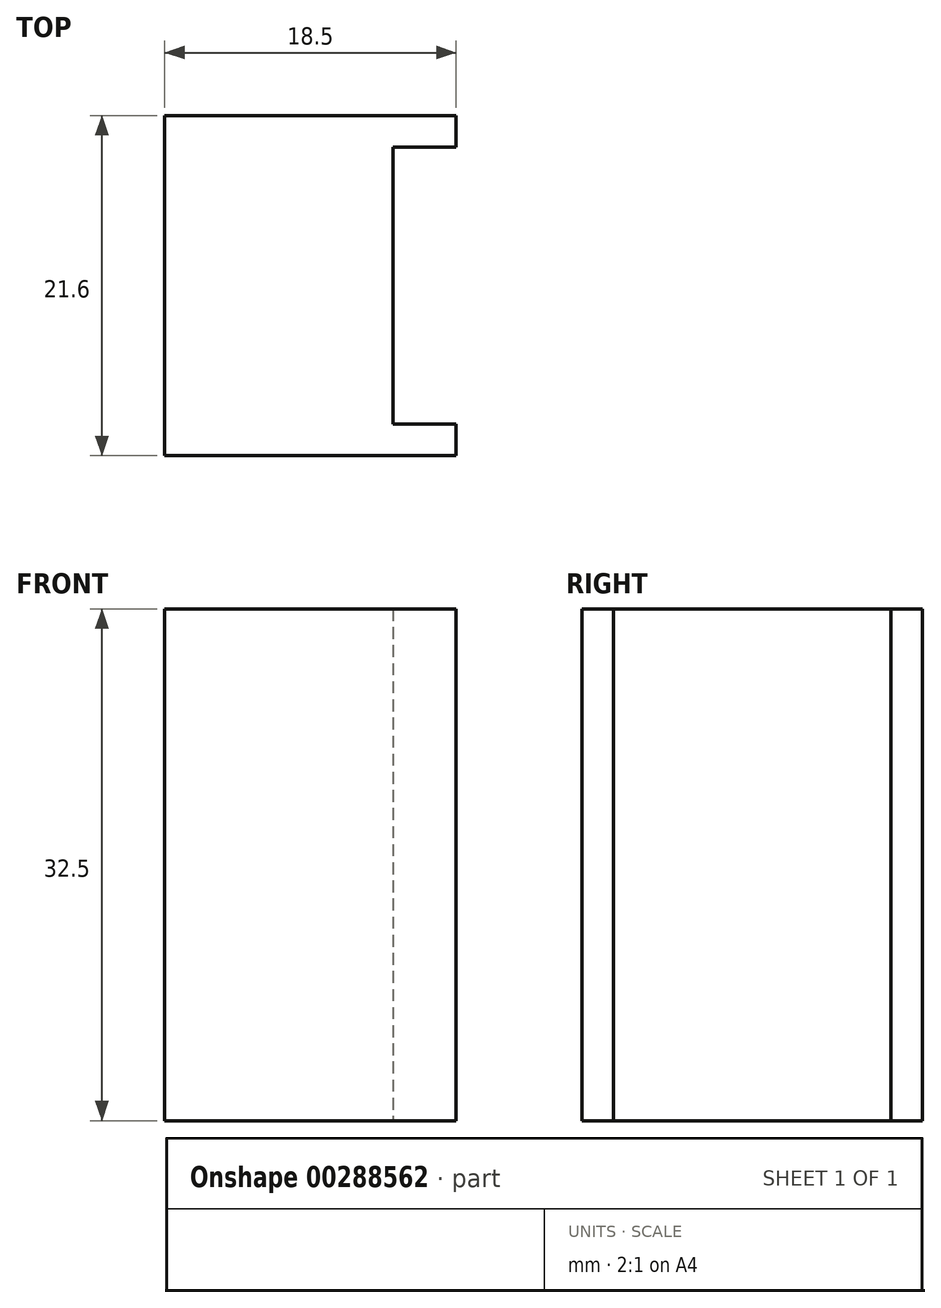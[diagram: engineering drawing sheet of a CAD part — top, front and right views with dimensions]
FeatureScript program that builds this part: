
annotation { "Feature Type Name" : "Feature", "Feature Type Description" : "" }
export const myFeature = defineFeature(function(context is Context, id is Id, definition is map)
    precondition{}
    {
        {
            var Q0;
            Q0=qCreatedBy(makeId("Top.planeOp"),FACE);
            var sketch = newSketch(context, id + "F0", { "sketchPlane" : qUnion([Q0])});
            skLineSegment(sketch, "E0.bottom", {"start": v(7.25, 10.8) * mm, "end": v(-7.25, 10.8) * mm});
            skLineSegment(sketch, "E0.top", {"start": v(7.25, -10.8) * mm, "end": v(-7.25, -10.8) * mm});
            skLineSegment(sketch, "E0.left", {"start": v(7.25, 10.8) * mm, "end": v(7.25, -10.8) * mm});
            skLineSegment(sketch, "E0.right", {"start": v(-7.25, 10.8) * mm, "end": v(-7.25, -10.8) * mm});
            skPoint(sketch, "E0.middle", {"position": v(0, 0) * mm});
            skLineSegment(sketch, "E1.bottom", {"start": v(7.25, 10.8) * mm, "end": v(11.25, 10.8) * mm});
            skLineSegment(sketch, "E1.top", {"start": v(7.25, 8.8) * mm, "end": v(11.25, 8.8) * mm});
            skLineSegment(sketch, "E1.left", {"start": v(7.25, 10.8) * mm, "end": v(7.25, 8.8) * mm});
            skLineSegment(sketch, "E1.right", {"start": v(11.25, 10.8) * mm, "end": v(11.25, 8.8) * mm});
            skLineSegment(sketch, "E2.MirrorCS", {"start": v(7.25, -8.8) * mm, "end": v(11.25, -8.8) * mm});
            skLineSegment(sketch, "E3.MirrorCS", {"start": v(7.25, -10.8) * mm, "end": v(11.25, -10.8) * mm});
            skLineSegment(sketch, "E4.MirrorCS", {"start": v(11.25, -10.8) * mm, "end": v(11.25, -8.8) * mm});
            skSolve(sketch);
        }
        {
            var Q0;
            {var subQ1=sQuery(id+"F0.wireOp",EDGE,"E0.bottom");Q0=makeQuery(id+"F0.imprint","IMPRINT",FACE,{"disambiguationData":[TD([[makeQuery(id+"F0.imprint","IMPRINT",EDGE,{"derivedFrom":subQ1}),1.0]])]});}
            var Q1;
            {var subQ0=sQuery(id+"F0.wireOp",EDGE,"E1.bottom");Q1=makeQuery(id+"F0.imprint","IMPRINT",FACE,{"disambiguationData":[TD([[makeQuery(id+"F0.imprint","IMPRINT",EDGE,{"derivedFrom":subQ0}),-1.0]])]});}
            var Q2;
            {var subQ2=sQuery(id+"F0.wireOp",EDGE,"E2.MirrorCS");Q2=makeQuery(id+"F0.imprint","IMPRINT",FACE,{"disambiguationData":[TD([[makeQuery(id+"F0.imprint","IMPRINT",EDGE,{"derivedFrom":subQ2}),-1.0]])]});}
            extrude(context, id + "F1", {"entities" : qUnion([Q0, Q1, Q2]), "depth" : 32.5 * mm, "offsetDistance" : 25 * mm});
        }
    });
